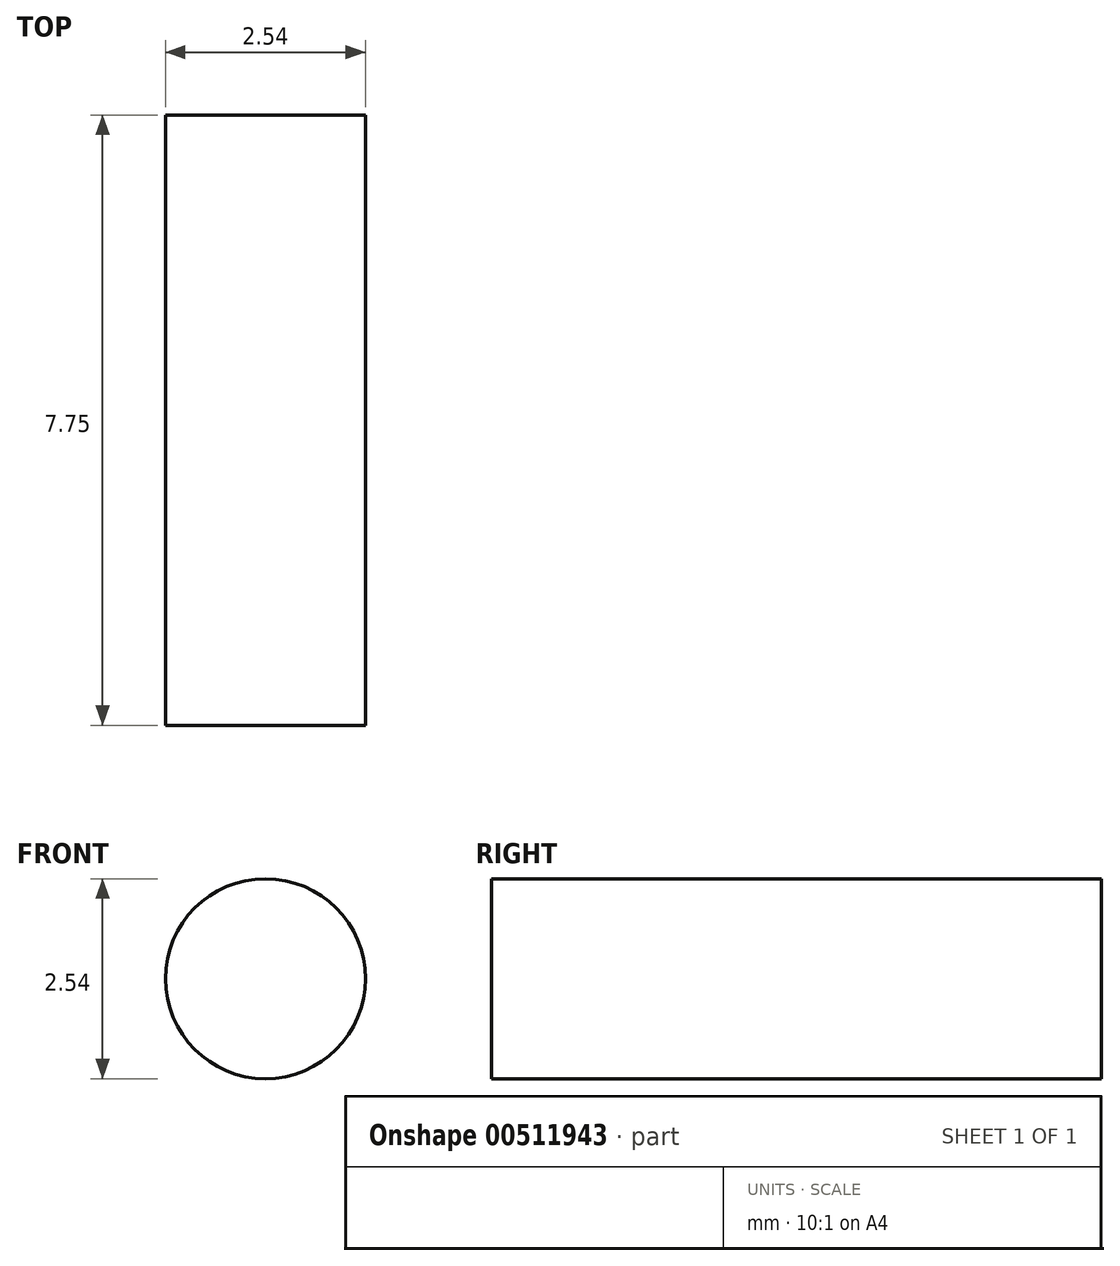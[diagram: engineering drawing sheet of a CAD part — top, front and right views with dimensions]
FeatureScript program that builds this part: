
annotation { "Feature Type Name" : "Feature", "Feature Type Description" : "" }
export const myFeature = defineFeature(function(context is Context, id is Id, definition is map)
    precondition{}
    {
        {
            assignVariable(context, id + "F0", {"name" : "X", "anyValue" : 6.25});
        }
        {
            var Q0;
            Q0=qCreatedBy(makeId("Front.planeOp"),FACE);
            var sketch = newSketch(context, id + "F1", { "sketchPlane" : qUnion([Q0])});
            skCircle(sketch, "E0", {"center": v(0, 0) * mm, "radius": 1.27 * mm});
            skSolve(sketch);
        }
        {
            var Q0;
            Q0=makeQuery(id+"F1.imprint","IMPRINT",FACE,{"disambiguationData":[TD([[makeQuery(id+"F1.imprint","IMPRINT",EDGE,{"derivedFrom":sQuery(id+"F1.wireOp",EDGE,"E0")}),1.0]])]});
            extrude(context, id + "F2", {"entities" : qUnion([Q0]), "depth" : (getVariable(context, 'X') + 1.5) * mm});
        }
    });
